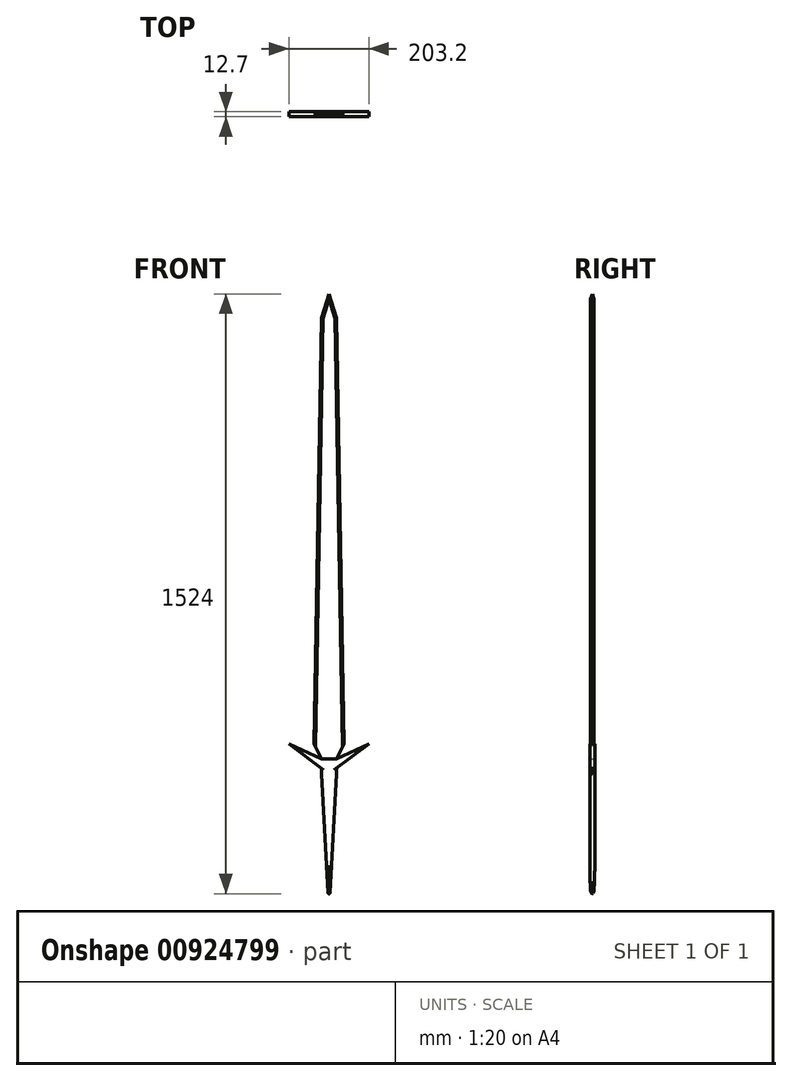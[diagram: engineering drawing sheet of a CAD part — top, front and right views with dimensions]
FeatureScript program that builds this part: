
annotation { "Feature Type Name" : "Feature", "Feature Type Description" : "" }
export const myFeature = defineFeature(function(context is Context, id is Id, definition is map)
    precondition{}
    {
        {
            var Q0;
            Q0=qCreatedBy(makeId("Front.planeOp"),FACE);
            var sketch = newSketch(context, id + "F0", { "sketchPlane" : qUnion([Q0])});
            skLineSegment(sketch, "E0", {"start": v(0, 0) * mm, "end": v(0, -348.84) * mm, "construction": true});
            skLineSegment(sketch, "E1", {"start": v(0, 0) * mm, "end": v(0, 1219.2) * mm, "construction": true});
            skLineSegment(sketch, "E2", {"start": v(0, 1219.2) * mm, "end": v(-19.05, 1157.45) * mm});
            skLineSegment(sketch, "E3", {"start": v(-19.05, 1157.45) * mm, "end": v(0, 1157.45) * mm, "construction": true});
            skLineSegment(sketch, "E4", {"start": v(0, 0) * mm, "end": v(0, 76.2) * mm, "construction": true});
            skLineSegment(sketch, "E5", {"start": v(0, 76.2) * mm, "end": v(-38.1, 76.2) * mm, "construction": true});
            skLineSegment(sketch, "E6", {"start": v(-38.1, 76.2) * mm, "end": v(-19.05, 38.1) * mm});
            skLineSegment(sketch, "E7", {"start": v(-38.1, 76.2) * mm, "end": v(-19.05, 1157.45) * mm});
            skLineSegment(sketch, "E8", {"start": v(-101.6, 0) * mm, "end": v(-101.6, 76.2) * mm, "construction": true});
            skLineSegment(sketch, "E9", {"start": v(-101.6, 76.2) * mm, "end": v(-19.05, 14.29) * mm});
            skLineSegment(sketch, "E10", {"start": v(-19.05, 38.1) * mm, "end": v(-101.6, 76.2) * mm});
            skLineSegment(sketch, "E11", {"start": v(-19.05, 14.29) * mm, "end": v(-19.05, 0) * mm});
            skLineSegment(sketch, "E12.MirrorCS", {"start": v(38.1, 76.2) * mm, "end": v(19.05, 1157.45) * mm});
            skLineSegment(sketch, "E13.MirrorCS", {"start": v(0, 1219.2) * mm, "end": v(19.05, 1157.45) * mm});
            skLineSegment(sketch, "E14.MirrorCS", {"start": v(38.1, 76.2) * mm, "end": v(19.05, 38.1) * mm});
            skLineSegment(sketch, "E15.MirrorCS", {"start": v(19.05, 38.1) * mm, "end": v(101.6, 76.2) * mm});
            skLineSegment(sketch, "E16.MirrorCS", {"start": v(101.6, 76.2) * mm, "end": v(19.05, 14.29) * mm});
            skLineSegment(sketch, "E17.MirrorCS", {"start": v(19.05, 14.29) * mm, "end": v(19.05, 0) * mm});
            skLineSegment(sketch, "E18", {"start": v(-19.05, 38.1) * mm, "end": v(19.05, 38.1) * mm});
            skPoint(sketch, "E19.orphan", {"position": v(0, 0) * mm});
            skLineSegment(sketch, "E20", {"start": v(0, 1219.2) * mm, "end": v(0, 1157.45) * mm, "construction": true});
            skLineSegment(sketch, "E21", {"start": v(-19.05, 0) * mm, "end": v(-2.54, -302.4) * mm});
            skLineSegment(sketch, "E22", {"start": v(19.05, 0) * mm, "end": v(2.54, -302.4) * mm});
            skPoint(sketch, "E23.visualSharp", {"position": v(0, -348.84) * mm});
            skArc(sketch, "E23.filletArc", {"start": v(-2.54, -302.4) * mm, "mid": v(0, -304.8) * mm, "end": v(2.54, -302.4) * mm});
            skLineSegment(sketch, "E24", {"start": v(19.05, 0) * mm, "end": v(19.05, -304.8) * mm, "construction": true});
            skPoint(sketch, "E24.endSnap0", {"position": v(0, -304.8) * mm});
            skSolve(sketch);
        }
        {
            var Q0;
            Q0=makeQuery(id+"F0.imprint","IMPRINT",FACE,{"disambiguationData":[TD([[makeQuery(id+"F0.imprint","IMPRINT",EDGE,{"derivedFrom":sQuery(id+"F0.wireOp",EDGE,"E2")}),1.0]])]});
            extrude(context, id + "F1", {"entities" : qUnion([Q0]), "endBound" : BoundingType.SYMMETRIC, "depth" : 7.94 * mm, "offsetDistance" : 25.4 * mm});
        }
        {
            var Q0;
            Q0=makeQuery(id+"F1.opExtrude","CAP_EDGE",EDGE,{"disambiguationData":[OSD([sQuery(id+"F0.wireOp",EDGE,"E2")])],"isStart":true});
            var Q1;
            Q1=makeQuery(id+"F1.opExtrude","CAP_EDGE",EDGE,{"disambiguationData":[OSD([sQuery(id+"F0.wireOp",EDGE,"E2")])],"isStart":false});
            chamfer(context, id + "F2", {"entities" : qUnion([Q0, Q1]), "width" : 3.97 * mm, "tangentPropagation" : true});
        }
        {
            var Q0;
            Q0=makeQuery(id+"F1.opExtrude","CAP_EDGE",EDGE,{"disambiguationData":[OSD([sQuery(id+"F0.wireOp",EDGE,"E7")])],"isStart":false});
            var Q1;
            Q1=makeQuery(id+"F1.opExtrude","CAP_EDGE",EDGE,{"disambiguationData":[OSD([sQuery(id+"F0.wireOp",EDGE,"E7")])],"isStart":true});
            chamfer(context, id + "F3", {"entities" : qUnion([Q0, Q1]), "width" : 3.97 * mm, "tangentPropagation" : true});
        }
        {
            var Q0;
            Q0=makeQuery(id+"F1.opExtrude","CAP_EDGE",EDGE,{"disambiguationData":[OSD([sQuery(id+"F0.wireOp",EDGE,"E13.MirrorCS")])],"isStart":false});
            var Q1;
            Q1=makeQuery(id+"F1.opExtrude","CAP_EDGE",EDGE,{"disambiguationData":[OSD([sQuery(id+"F0.wireOp",EDGE,"E13.MirrorCS")])],"isStart":true});
            chamfer(context, id + "F4", {"entities" : qUnion([Q0, Q1]), "width" : 3.96 * mm, "tangentPropagation" : true});
        }
        {
            var Q0;
            Q0=makeQuery(id+"F1.opExtrude","CAP_EDGE",EDGE,{"disambiguationData":[OSD([sQuery(id+"F0.wireOp",EDGE,"E12.MirrorCS")])],"isStart":false});
            var Q1;
            Q1=makeQuery(id+"F1.opExtrude","CAP_EDGE",EDGE,{"disambiguationData":[OSD([sQuery(id+"F0.wireOp",EDGE,"E12.MirrorCS")])],"isStart":true});
            chamfer(context, id + "F5", {"entities" : qUnion([Q0, Q1]), "width" : 3.96 * mm, "tangentPropagation" : true});
        }
        {
            var Q0;
            Q0=makeQuery(id+"F0.imprint","IMPRINT",FACE,{"disambiguationData":[TD([[makeQuery(id+"F0.imprint","IMPRINT",EDGE,{"derivedFrom":sQuery(id+"F0.wireOp",EDGE,"E9")}),1.0]])]});
            extrude(context, id + "F6", {"entities" : qUnion([Q0]), "endBound" : BoundingType.SYMMETRIC, "depth" : 12.7 * mm, "offsetDistance" : 25.4 * mm});
        }
        {
            var Q0;
            Q0=makeQuery(id+"F6.opExtrude","CAP_EDGE",EDGE,{"disambiguationData":[OSD([sQuery(id+"F0.wireOp",EDGE,"E22")])],"isStart":false});
            var Q1;
            Q1=makeQuery(id+"F6.opExtrude","CAP_EDGE",EDGE,{"disambiguationData":[OSD([sQuery(id+"F0.wireOp",EDGE,"E21")])],"isStart":false});
            var Q2;
            Q2=makeQuery(id+"F6.opExtrude","CAP_EDGE",EDGE,{"disambiguationData":[OSD([sQuery(id+"F0.wireOp",EDGE,"E21")])],"isStart":true});
            fillet(context, id + "F7", {"entities" : qUnion([Q0, Q1, Q2]), "radius" : 6.35 * mm, "tangentPropagation" : true, "allowEdgeOverflow" : false});
        }
    });
